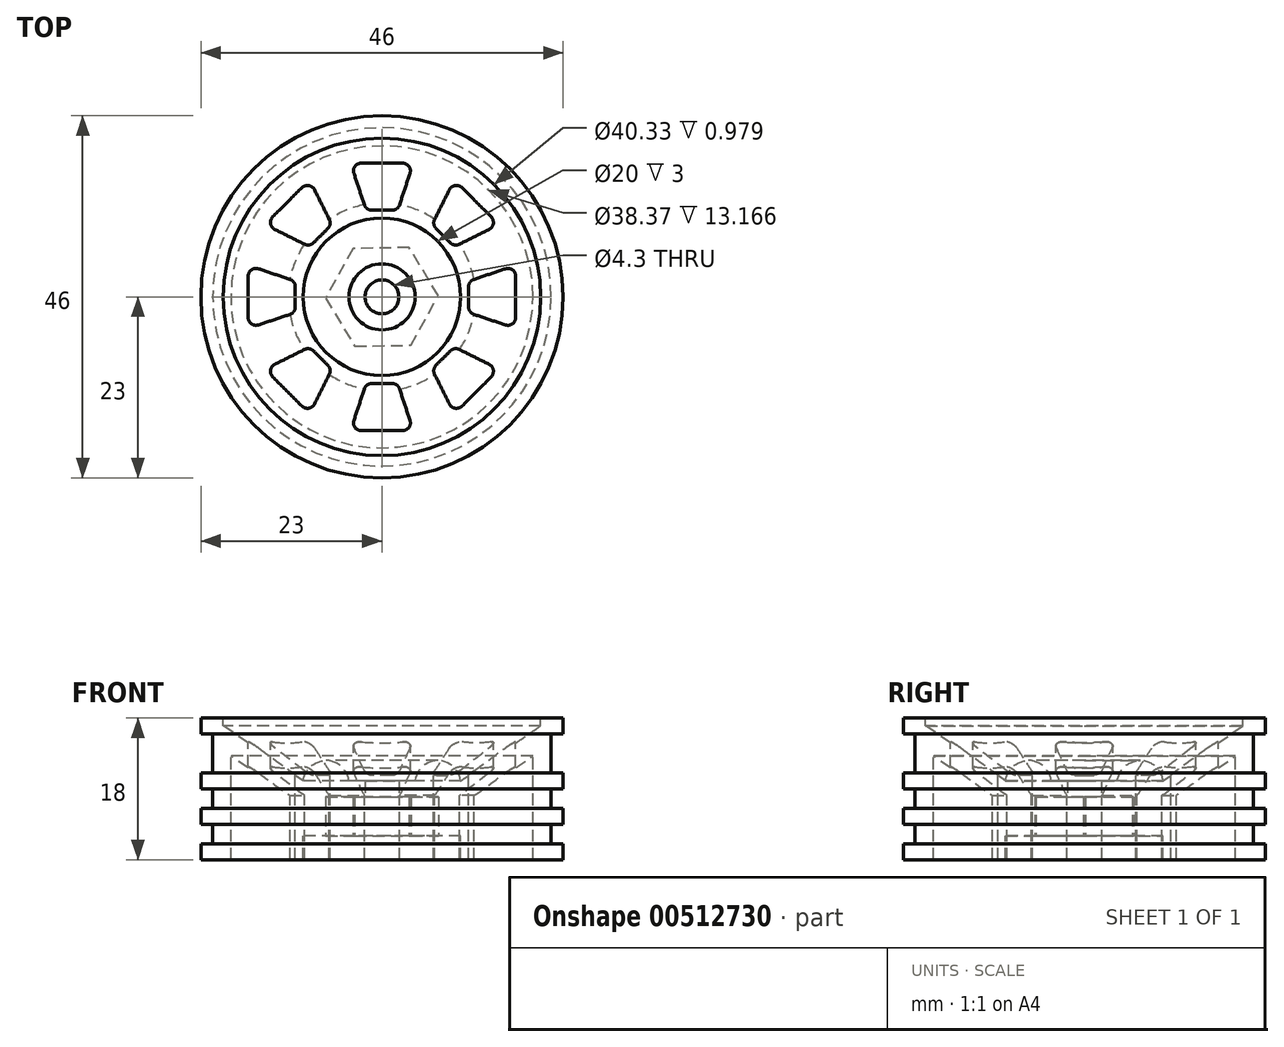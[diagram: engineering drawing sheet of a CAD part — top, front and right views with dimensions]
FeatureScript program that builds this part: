
annotation { "Feature Type Name" : "Feature", "Feature Type Description" : "" }
export const myFeature = defineFeature(function(context is Context, id is Id, definition is map)
    precondition{}
    {
        {
            var Q0;
            Q0=qCreatedBy(makeId("Front.planeOp"),FACE);
            var sketch = newSketch(context, id + "F0", { "sketchPlane" : qUnion([Q0])});
            skLineSegment(sketch, "E0", {"start": v(10, 0) * mm, "end": v(10.72, 0) * mm});
            skLineSegment(sketch, "E1", {"start": v(23, 0) * mm, "end": v(23, 2) * mm});
            skLineSegment(sketch, "E2", {"start": v(21.5, 2) * mm, "end": v(21.5, 4.5) * mm});
            skLineSegment(sketch, "E3", {"start": v(21.5, 2) * mm, "end": v(23, 2) * mm});
            skLineSegment(sketch, "E4", {"start": v(23, 4.5) * mm, "end": v(21.5, 4.5) * mm});
            skLineSegment(sketch, "E5", {"start": v(21.5, 6.5) * mm, "end": v(21.5, 9) * mm});
            skLineSegment(sketch, "E6", {"start": v(21.78, 16) * mm, "end": v(23, 16) * mm});
            skLineSegment(sketch, "E7", {"start": v(23, 16) * mm, "end": v(23, 18) * mm});
            skLineSegment(sketch, "E8", {"start": v(23, 18) * mm, "end": v(20.17, 18) * mm});
            skLineSegment(sketch, "E9", {"start": v(0, 10) * mm, "end": v(0, 3) * mm});
            skPoint(sketch, "E10.endSnap0", {"position": v(17.5, 18) * mm});
            skLineSegment(sketch, "E11", {"start": v(17.92, 15.47) * mm, "end": v(10, 10) * mm});
            skLineSegment(sketch, "E12", {"start": v(4.2, 10) * mm, "end": v(0, 10) * mm});
            skPoint(sketch, "E13.start.orphan", {"position": v(12, 18) * mm});
            skPoint(sketch, "E14.end.orphan", {"position": v(10.72, 0) * mm});
            skLineSegment(sketch, "E15", {"start": v(10, 3) * mm, "end": v(10, 0) * mm});
            skLineSegment(sketch, "E16.trimOffspring", {"start": v(19.19, 0) * mm, "end": v(23, 0) * mm});
            skLineSegment(sketch, "E17", {"start": v(23, 4.5) * mm, "end": v(23, 6.5) * mm});
            skLineSegment(sketch, "E18", {"start": v(23, 6.5) * mm, "end": v(21.5, 6.5) * mm});
            skPoint(sketch, "E19.end.orphan", {"position": v(21.5, -0.75) * mm});
            skPoint(sketch, "E20.end.orphan", {"position": v(26.5, 17) * mm});
            skPoint(sketch, "E21.end.orphan", {"position": v(23, 15) * mm});
            skLineSegment(sketch, "E22", {"start": v(21.5, 11) * mm, "end": v(23, 11) * mm});
            skLineSegment(sketch, "E23", {"start": v(23, 11) * mm, "end": v(23, 9) * mm});
            skLineSegment(sketch, "E24", {"start": v(23, 9) * mm, "end": v(21.5, 9) * mm});
            skLineSegment(sketch, "E25.trimOffspring", {"start": v(21.5, 11) * mm, "end": v(21.5, 15.72) * mm});
            skLineSegment(sketch, "E26.trimOffspring", {"start": v(21.5, 11) * mm, "end": v(21.5, 11) * mm});
            skPoint(sketch, "E27.visualSharp", {"position": v(17.5, 13.9) * mm});
            skPoint(sketch, "E28.visualSharp", {"position": v(20, 18) * mm});
            skPoint(sketch, "E29.start.orphan", {"position": v(21.5, 11) * mm});
            skPoint(sketch, "E30.visualSharp", {"position": v(21.5, 16) * mm});
            skArc(sketch, "E30.filletArc", {"start": v(21.78, 16) * mm, "mid": v(21.58, 15.92) * mm, "end": v(21.5, 15.72) * mm});
            skPoint(sketch, "E31.orphan", {"position": v(0, 21) * mm});
            skLineSegment(sketch, "E32", {"start": v(10, 10) * mm, "end": v(20.17, 17.02) * mm});
            skLineSegment(sketch, "E33", {"start": v(20.17, 18) * mm, "end": v(20.17, 17.02) * mm});
            skLineSegment(sketch, "E34", {"start": v(19.19, 12.15) * mm, "end": v(19.19, 0) * mm});
            skPoint(sketch, "E35.orphan", {"position": v(17.92, 0) * mm});
            skPoint(sketch, "E36.orphan", {"position": v(19.19, 13.9) * mm});
            skLineSegment(sketch, "E37", {"start": v(19.19, 12.15) * mm, "end": v(19.19, 13.17) * mm});
            skLineSegment(sketch, "E38", {"start": v(11.9, 8.14) * mm, "end": v(19.19, 13.17) * mm});
            skPoint(sketch, "E39.1.end.orphan", {"position": v(11.08, 6.55) * mm});
            skPoint(sketch, "E40.start.orphan", {"position": v(17.92, 11.28) * mm});
            skLineSegment(sketch, "E41", {"start": v(11.9, 8) * mm, "end": v(11.9, 0) * mm});
            skLineSegment(sketch, "E42", {"start": v(10, 0) * mm, "end": v(11.9, 0) * mm});
            skPoint(sketch, "E43.orphan", {"position": v(11.08, 7.57) * mm});
            skLineSegment(sketch, "E44", {"start": v(10, 0) * mm, "end": v(10, 3) * mm});
            skLineSegment(sketch, "E45", {"start": v(10, 3) * mm, "end": v(0, 3) * mm});
            skLineSegment(sketch, "E46", {"start": v(11.9, 8) * mm, "end": v(11.9, 8.14) * mm});
            skArc(sketch, "E47", {"start": v(10, 10) * mm, "mid": v(7.1, 12.6) * mm, "end": v(4.2, 10) * mm});
            skSolve(sketch);
        }
        {
            var Q0;
            Q0=makeQuery(id+"F0.imprint","IMPRINT",FACE,{"disambiguationData":[TD([[makeQuery(id+"F0.imprint","IMPRINT",EDGE,{"derivedFrom":sQuery(id+"F0.wireOp",EDGE,"E1")}),1.0]])]});
            var Q1;
            Q1=sQuery(id+"F0.wireOp",EDGE,"E9");
            revolve(context, id + "F1", {"entities" : qUnion([Q0]), "axis" : qUnion([Q1]), "revolveType" : RevolveType.FULL});
        }
        {
            var Q0;
            Q0=makeQuery(id+"F1.opRevolve","SWEPT_FACE",FACE,{"disambiguationData":[OSD([sQuery(id+"F0.wireOp",EDGE,"E8")])]});
            cPlane(context, id + "F2", {"entities" : qUnion([Q0]), "cplaneType" : CPlaneType.OFFSET, "offset" : 25 * mm, "width" : 150 * mm, "height" : 150 * mm});
        }
        {
            var Q0;
            Q0=qCreatedBy(id+"F2.planeOp",FACE);
            var sketch = newSketch(context, id + "F3", { "sketchPlane" : qUnion([Q0])});
            skLineSegment(sketch, "E48", {"start": v(-2.61, 17) * mm, "end": v(2.61, 17) * mm});
            skLineSegment(sketch, "E49", {"start": v(3.56, 15.68) * mm, "end": v(2.23, 11.68) * mm});
            skLineSegment(sketch, "E50", {"start": v(1.28, 11) * mm, "end": v(-1.28, 11) * mm});
            skLineSegment(sketch, "E51", {"start": v(-2.23, 11.68) * mm, "end": v(-3.56, 15.68) * mm});
            skPoint(sketch, "E52.visualSharp", {"position": v(-4, 17) * mm});
            skArc(sketch, "E52.filletArc", {"start": v(-2.61, 17) * mm, "mid": v(-3.42, 16.58) * mm, "end": v(-3.56, 15.68) * mm});
            skPoint(sketch, "E53.visualSharp", {"position": v(-2, 11) * mm});
            skArc(sketch, "E53.filletArc", {"start": v(-2.23, 11.68) * mm, "mid": v(-1.86, 11.19) * mm, "end": v(-1.28, 11) * mm});
            skPoint(sketch, "E54.visualSharp", {"position": v(2, 11) * mm});
            skArc(sketch, "E54.filletArc", {"start": v(1.28, 11) * mm, "mid": v(1.86, 11.19) * mm, "end": v(2.23, 11.68) * mm});
            skPoint(sketch, "E55.visualSharp", {"position": v(4, 17) * mm});
            skArc(sketch, "E55.filletArc", {"start": v(3.56, 15.68) * mm, "mid": v(3.42, 16.58) * mm, "end": v(2.61, 17) * mm});
            skLineSegment(sketch, "E56.1.0", {"start": v(-9.84, 6.69) * mm, "end": v(-13.6, 8.57) * mm});
            skLineSegment(sketch, "E56.1.1", {"start": v(-13.87, 10.17) * mm, "end": v(-10.17, 13.87) * mm});
            skLineSegment(sketch, "E56.1.2", {"start": v(-8.57, 13.6) * mm, "end": v(-6.69, 9.84) * mm});
            skLineSegment(sketch, "E56.1.3", {"start": v(-6.87, 8.68) * mm, "end": v(-8.68, 6.87) * mm});
            skArc(sketch, "E56.1.4", {"start": v(-6.87, 8.68) * mm, "mid": v(-6.6, 9.23) * mm, "end": v(-6.69, 9.84) * mm});
            skArc(sketch, "E56.1.5", {"start": v(-9.84, 6.69) * mm, "mid": v(-9.23, 6.6) * mm, "end": v(-8.68, 6.87) * mm});
            skArc(sketch, "E56.1.6", {"start": v(-8.57, 13.6) * mm, "mid": v(-9.3, 14.15) * mm, "end": v(-10.17, 13.87) * mm});
            skArc(sketch, "E56.1.7", {"start": v(-13.87, 10.17) * mm, "mid": v(-14.15, 9.3) * mm, "end": v(-13.6, 8.57) * mm});
            skLineSegment(sketch, "E56.2.0", {"start": v(-11.68, -2.23) * mm, "end": v(-15.68, -3.56) * mm});
            skLineSegment(sketch, "E56.2.1", {"start": v(-17, -2.61) * mm, "end": v(-17, 2.61) * mm});
            skLineSegment(sketch, "E56.2.2", {"start": v(-15.68, 3.56) * mm, "end": v(-11.68, 2.23) * mm});
            skLineSegment(sketch, "E56.2.3", {"start": v(-11, 1.28) * mm, "end": v(-11, -1.28) * mm});
            skArc(sketch, "E56.2.4", {"start": v(-11, 1.28) * mm, "mid": v(-11.19, 1.86) * mm, "end": v(-11.68, 2.23) * mm});
            skArc(sketch, "E56.2.5", {"start": v(-11.68, -2.23) * mm, "mid": v(-11.19, -1.86) * mm, "end": v(-11, -1.28) * mm});
            skArc(sketch, "E56.2.6", {"start": v(-15.68, 3.56) * mm, "mid": v(-16.58, 3.42) * mm, "end": v(-17, 2.61) * mm});
            skArc(sketch, "E56.2.7", {"start": v(-17, -2.61) * mm, "mid": v(-16.58, -3.42) * mm, "end": v(-15.68, -3.56) * mm});
            skLineSegment(sketch, "E56.3.0", {"start": v(-6.69, -9.84) * mm, "end": v(-8.57, -13.6) * mm});
            skLineSegment(sketch, "E56.3.1", {"start": v(-10.17, -13.87) * mm, "end": v(-13.87, -10.17) * mm});
            skLineSegment(sketch, "E56.3.2", {"start": v(-13.6, -8.57) * mm, "end": v(-9.84, -6.69) * mm});
            skLineSegment(sketch, "E56.3.3", {"start": v(-8.68, -6.87) * mm, "end": v(-6.87, -8.68) * mm});
            skArc(sketch, "E56.3.4", {"start": v(-8.68, -6.87) * mm, "mid": v(-9.23, -6.6) * mm, "end": v(-9.84, -6.69) * mm});
            skArc(sketch, "E56.3.5", {"start": v(-6.69, -9.84) * mm, "mid": v(-6.6, -9.23) * mm, "end": v(-6.87, -8.68) * mm});
            skArc(sketch, "E56.3.6", {"start": v(-13.6, -8.57) * mm, "mid": v(-14.15, -9.3) * mm, "end": v(-13.87, -10.17) * mm});
            skArc(sketch, "E56.3.7", {"start": v(-10.17, -13.87) * mm, "mid": v(-9.3, -14.15) * mm, "end": v(-8.57, -13.6) * mm});
            skLineSegment(sketch, "E56.4.0", {"start": v(2.23, -11.68) * mm, "end": v(3.56, -15.68) * mm});
            skLineSegment(sketch, "E56.4.1", {"start": v(2.61, -17) * mm, "end": v(-2.61, -17) * mm});
            skLineSegment(sketch, "E56.4.2", {"start": v(-3.56, -15.68) * mm, "end": v(-2.23, -11.68) * mm});
            skLineSegment(sketch, "E56.4.3", {"start": v(-1.28, -11) * mm, "end": v(1.28, -11) * mm});
            skArc(sketch, "E56.4.4", {"start": v(-1.28, -11) * mm, "mid": v(-1.86, -11.19) * mm, "end": v(-2.23, -11.68) * mm});
            skArc(sketch, "E56.4.5", {"start": v(2.23, -11.68) * mm, "mid": v(1.86, -11.19) * mm, "end": v(1.28, -11) * mm});
            skArc(sketch, "E56.4.6", {"start": v(-3.56, -15.68) * mm, "mid": v(-3.42, -16.58) * mm, "end": v(-2.61, -17) * mm});
            skArc(sketch, "E56.4.7", {"start": v(2.61, -17) * mm, "mid": v(3.42, -16.58) * mm, "end": v(3.56, -15.68) * mm});
            skLineSegment(sketch, "E56.5.0", {"start": v(9.84, -6.69) * mm, "end": v(13.6, -8.57) * mm});
            skLineSegment(sketch, "E56.5.1", {"start": v(13.87, -10.17) * mm, "end": v(10.17, -13.87) * mm});
            skLineSegment(sketch, "E56.5.2", {"start": v(8.57, -13.6) * mm, "end": v(6.69, -9.84) * mm});
            skLineSegment(sketch, "E56.5.3", {"start": v(6.87, -8.68) * mm, "end": v(8.68, -6.87) * mm});
            skArc(sketch, "E56.5.4", {"start": v(6.87, -8.68) * mm, "mid": v(6.6, -9.23) * mm, "end": v(6.69, -9.84) * mm});
            skArc(sketch, "E56.5.5", {"start": v(9.84, -6.69) * mm, "mid": v(9.23, -6.6) * mm, "end": v(8.68, -6.87) * mm});
            skArc(sketch, "E56.5.6", {"start": v(8.57, -13.6) * mm, "mid": v(9.3, -14.15) * mm, "end": v(10.17, -13.87) * mm});
            skArc(sketch, "E56.5.7", {"start": v(13.87, -10.17) * mm, "mid": v(14.15, -9.3) * mm, "end": v(13.6, -8.57) * mm});
            skLineSegment(sketch, "E56.6.0", {"start": v(11.68, 2.23) * mm, "end": v(15.68, 3.56) * mm});
            skLineSegment(sketch, "E56.6.1", {"start": v(17, 2.61) * mm, "end": v(17, -2.61) * mm});
            skLineSegment(sketch, "E56.6.2", {"start": v(15.68, -3.56) * mm, "end": v(11.68, -2.23) * mm});
            skLineSegment(sketch, "E56.6.3", {"start": v(11, -1.28) * mm, "end": v(11, 1.28) * mm});
            skArc(sketch, "E56.6.4", {"start": v(11, -1.28) * mm, "mid": v(11.19, -1.86) * mm, "end": v(11.68, -2.23) * mm});
            skArc(sketch, "E56.6.5", {"start": v(11.68, 2.23) * mm, "mid": v(11.19, 1.86) * mm, "end": v(11, 1.28) * mm});
            skArc(sketch, "E56.6.6", {"start": v(15.68, -3.56) * mm, "mid": v(16.58, -3.42) * mm, "end": v(17, -2.61) * mm});
            skArc(sketch, "E56.6.7", {"start": v(17, 2.61) * mm, "mid": v(16.58, 3.42) * mm, "end": v(15.68, 3.56) * mm});
            skLineSegment(sketch, "E56.7.0", {"start": v(6.69, 9.84) * mm, "end": v(8.57, 13.6) * mm});
            skLineSegment(sketch, "E56.7.1", {"start": v(10.17, 13.87) * mm, "end": v(13.87, 10.17) * mm});
            skLineSegment(sketch, "E56.7.2", {"start": v(13.6, 8.57) * mm, "end": v(9.84, 6.69) * mm});
            skLineSegment(sketch, "E56.7.3", {"start": v(8.68, 6.87) * mm, "end": v(6.87, 8.68) * mm});
            skArc(sketch, "E56.7.4", {"start": v(8.68, 6.87) * mm, "mid": v(9.23, 6.6) * mm, "end": v(9.84, 6.69) * mm});
            skArc(sketch, "E56.7.5", {"start": v(6.69, 9.84) * mm, "mid": v(6.6, 9.23) * mm, "end": v(6.87, 8.68) * mm});
            skArc(sketch, "E56.7.6", {"start": v(13.6, 8.57) * mm, "mid": v(14.15, 9.3) * mm, "end": v(13.87, 10.17) * mm});
            skArc(sketch, "E56.7.7", {"start": v(10.17, 13.87) * mm, "mid": v(9.3, 14.15) * mm, "end": v(8.57, 13.6) * mm});
            skPoint(sketch, "E56.center", {"position": v(0, 0) * mm});
            skSolve(sketch);
        }
        {
            var Q0;
            Q0=makeQuery(id+"F3.imprint","IMPRINT",FACE,{"disambiguationData":[TD([[makeQuery(id+"F3.imprint","IMPRINT",EDGE,{"derivedFrom":sQuery(id+"F3.wireOp",EDGE,"E48")}),-1.0]])]});
            var Q1;
            Q1=makeQuery(id+"F3.imprint","IMPRINT",FACE,{"disambiguationData":[TD([[makeQuery(id+"F3.imprint","IMPRINT",EDGE,{"derivedFrom":sQuery(id+"F3.wireOp",EDGE,"E56.1.0")}),-1.0]])]});
            var Q2;
            Q2=makeQuery(id+"F3.imprint","IMPRINT",FACE,{"disambiguationData":[TD([[makeQuery(id+"F3.imprint","IMPRINT",EDGE,{"derivedFrom":sQuery(id+"F3.wireOp",EDGE,"E56.2.0")}),-1.0]])]});
            var Q3;
            Q3=makeQuery(id+"F3.imprint","IMPRINT",FACE,{"disambiguationData":[TD([[makeQuery(id+"F3.imprint","IMPRINT",EDGE,{"derivedFrom":sQuery(id+"F3.wireOp",EDGE,"E56.3.0")}),-1.0]])]});
            var Q4;
            Q4=makeQuery(id+"F3.imprint","IMPRINT",FACE,{"disambiguationData":[TD([[makeQuery(id+"F3.imprint","IMPRINT",EDGE,{"derivedFrom":sQuery(id+"F3.wireOp",EDGE,"E56.4.0")}),-1.0]])]});
            var Q5;
            Q5=makeQuery(id+"F3.imprint","IMPRINT",FACE,{"disambiguationData":[TD([[makeQuery(id+"F3.imprint","IMPRINT",EDGE,{"derivedFrom":sQuery(id+"F3.wireOp",EDGE,"E56.5.0")}),-1.0]])]});
            var Q6;
            Q6=makeQuery(id+"F3.imprint","IMPRINT",FACE,{"disambiguationData":[TD([[makeQuery(id+"F3.imprint","IMPRINT",EDGE,{"derivedFrom":sQuery(id+"F3.wireOp",EDGE,"E56.6.0")}),-1.0]])]});
            var Q7;
            Q7=makeQuery(id+"F3.imprint","IMPRINT",FACE,{"disambiguationData":[TD([[makeQuery(id+"F3.imprint","IMPRINT",EDGE,{"derivedFrom":sQuery(id+"F3.wireOp",EDGE,"E56.7.0")}),-1.0]])]});
            extrude(context, id + "F4", {"entities" : qUnion([Q0, Q1, Q2, Q3, Q4, Q5, Q6, Q7]), "operationType" : NewBodyOperationType.REMOVE, "endBound" : BoundingType.THROUGH_ALL, "oppositeDirection" : true, "depth" : 25 * mm});
        }
        {
            var Q0;
            Q0=makeQuery(id+"F1.opRevolve","SWEPT_FACE",FACE,{"disambiguationData":[OSD([sQuery(id+"F0.wireOp",EDGE,"E12")])]});
            var sketch = newSketch(context, id + "F5", { "sketchPlane" : qUnion([Q0])});
            skCircle(sketch, "E57", {"center": v(0, 6.5) * mm, "radius": 0.75 * mm});
            skCircle(sketch, "E58.1.0", {"center": v(-5.63, 3.25) * mm, "radius": 0.75 * mm});
            skCircle(sketch, "E58.2.0", {"center": v(-5.63, -3.25) * mm, "radius": 0.75 * mm});
            skCircle(sketch, "E58.3.0", {"center": v(0, -6.5) * mm, "radius": 0.75 * mm});
            skCircle(sketch, "E58.4.0", {"center": v(5.63, -3.25) * mm, "radius": 0.75 * mm});
            skCircle(sketch, "E58.5.0", {"center": v(5.63, 3.25) * mm, "radius": 0.75 * mm});
            skPoint(sketch, "E58.center", {"position": v(0, 0) * mm});
            skSolve(sketch);
        }
        {
            var Q0;
            Q0=makeQuery(id+"F5.imprint","IMPRINT",FACE,{"disambiguationData":[TD([[makeQuery(id+"F5.imprint","IMPRINT",EDGE,{"derivedFrom":sQuery(id+"F5.wireOp",EDGE,"E57")}),1.0]])]});
            var Q1;
            Q1=makeQuery(id+"F5.imprint","IMPRINT",FACE,{"disambiguationData":[TD([[makeQuery(id+"F5.imprint","IMPRINT",EDGE,{"derivedFrom":sQuery(id+"F5.wireOp",EDGE,"E58.1.0")}),1.0]])]});
            var Q2;
            Q2=makeQuery(id+"F5.imprint","IMPRINT",FACE,{"disambiguationData":[TD([[makeQuery(id+"F5.imprint","IMPRINT",EDGE,{"derivedFrom":sQuery(id+"F5.wireOp",EDGE,"E58.2.0")}),1.0]])]});
            var Q3;
            Q3=makeQuery(id+"F5.imprint","IMPRINT",FACE,{"disambiguationData":[TD([[makeQuery(id+"F5.imprint","IMPRINT",EDGE,{"derivedFrom":sQuery(id+"F5.wireOp",EDGE,"E58.3.0")}),1.0]])]});
            var Q4;
            Q4=makeQuery(id+"F5.imprint","IMPRINT",FACE,{"disambiguationData":[TD([[makeQuery(id+"F5.imprint","IMPRINT",EDGE,{"derivedFrom":sQuery(id+"F5.wireOp",EDGE,"E58.4.0")}),1.0]])]});
            var Q5;
            Q5=makeQuery(id+"F5.imprint","IMPRINT",FACE,{"disambiguationData":[TD([[makeQuery(id+"F5.imprint","IMPRINT",EDGE,{"derivedFrom":sQuery(id+"F5.wireOp",EDGE,"E58.5.0")}),1.0]])]});
            extrude(context, id + "F6", {"entities" : qUnion([Q0, Q1, Q2, Q3, Q4, Q5]), "operationType" : NewBodyOperationType.ADD, "depth" : 1.5 * mm});
        }
        {
            var Q0;
            Q0=makeQuery(id+"F1.opRevolve","SWEPT_FACE",FACE,{"disambiguationData":[OSD([sQuery(id+"F0.wireOp",EDGE,"E45")])]});
            var sketch = newSketch(context, id + "F7", { "sketchPlane" : qUnion([Q0])});
            skCircle(sketch, "E59.cCircle", {"center": v(0, 0) * mm, "radius": 6.2 * mm, "construction": true});
            skLineSegment(sketch, "E59.0", {"start": v(7.16, -0.13) * mm, "end": v(3.47, -6.26) * mm});
            skLineSegment(sketch, "E59.1", {"start": v(3.47, -6.26) * mm, "end": v(-3.69, -6.14) * mm});
            skLineSegment(sketch, "E59.2", {"start": v(-3.69, -6.14) * mm, "end": v(-7.16, 0.13) * mm});
            skLineSegment(sketch, "E59.3", {"start": v(-7.16, 0.13) * mm, "end": v(-3.47, 6.26) * mm});
            skLineSegment(sketch, "E59.4", {"start": v(-3.47, 6.26) * mm, "end": v(3.69, 6.14) * mm});
            skLineSegment(sketch, "E59.5", {"start": v(3.69, 6.14) * mm, "end": v(7.16, -0.13) * mm});
            skPoint(sketch, "E59.0.midPoint", {"position": v(5.31, -3.2) * mm});
            skCircle(sketch, "E60", {"center": v(0, 0) * mm, "radius": 2.15 * mm});
            skSolve(sketch);
        }
        {
            var Q0;
            Q0=makeQuery(id+"F7.imprint","IMPRINT",FACE,{"disambiguationData":[TD([[makeQuery(id+"F7.imprint","IMPRINT",EDGE,{"derivedFrom":sQuery(id+"F7.wireOp",EDGE,"E59.0")}),-1.0]])]});
            extrude(context, id + "F8", {"entities" : qUnion([Q0]), "operationType" : NewBodyOperationType.REMOVE, "oppositeDirection" : true, "depth" : 5 * mm});
        }
        {
            var Q0;
            Q0=makeQuery(id+"F8.boolean.opBoolean","SPLIT",FACE,{"disambiguationData":[TD([makeQuery(id+"F8.opExtrude","SWEPT_FACE",FACE,{"disambiguationData":[OSD([sQuery(id+"F7.wireOp",EDGE,"E60")])]})])],"derivedFrom":makeQuery(id+"F1.opRevolve","SWEPT_FACE",FACE,{"disambiguationData":[OSD([sQuery(id+"F0.wireOp",EDGE,"E45")])]})});
            extrude(context, id + "F9", {"entities" : qUnion([Q0]), "operationType" : NewBodyOperationType.REMOVE, "endBound" : BoundingType.THROUGH_ALL, "oppositeDirection" : true, "depth" : 25 * mm});
        }
    });
